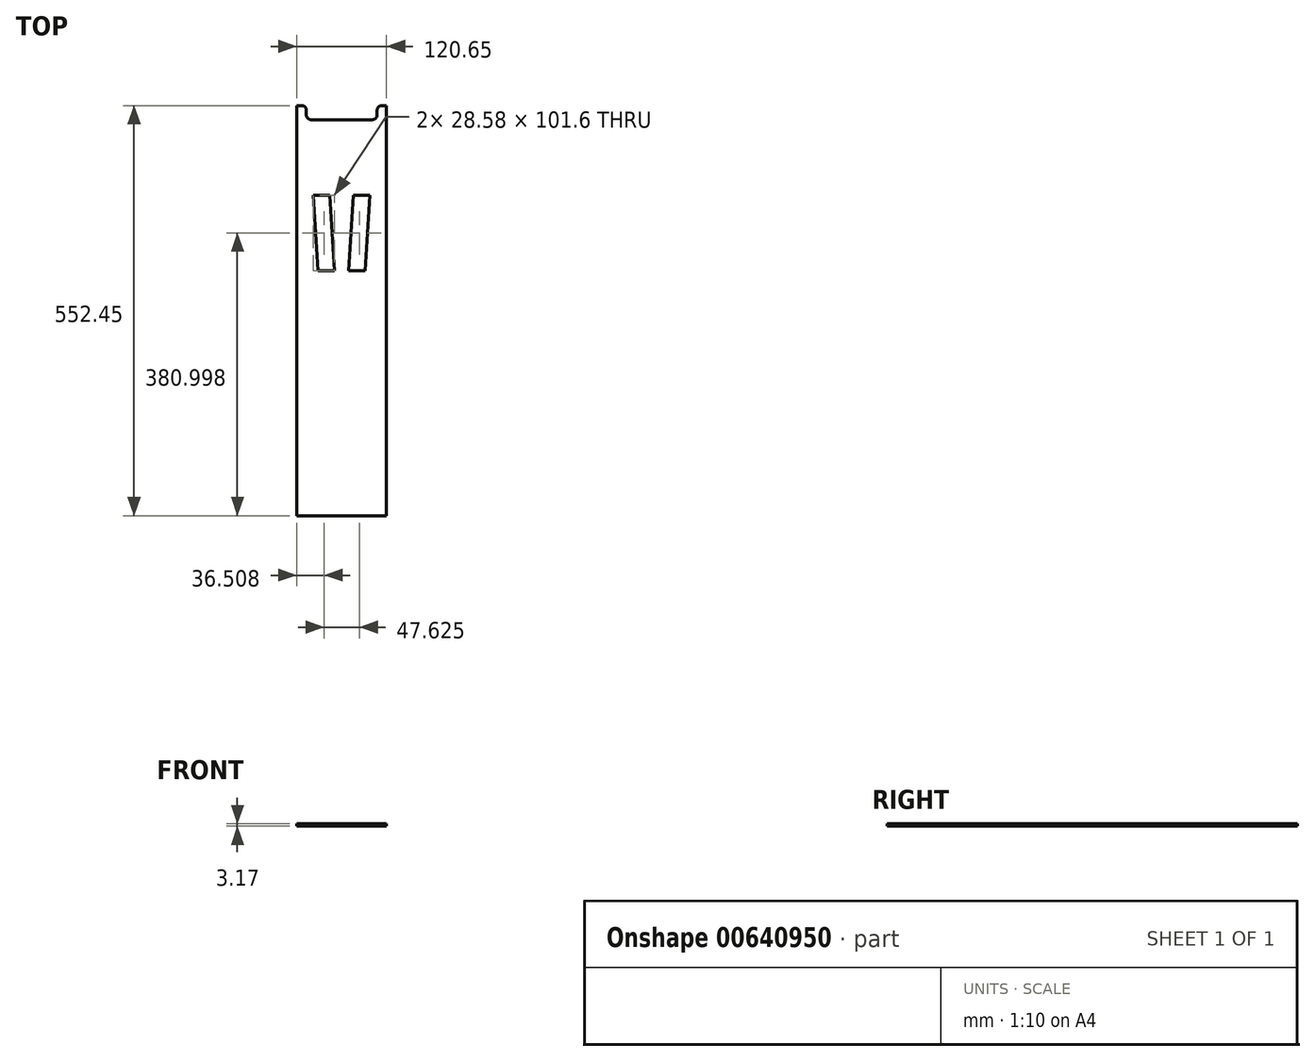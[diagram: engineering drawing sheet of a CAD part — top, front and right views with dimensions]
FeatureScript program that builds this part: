
annotation { "Feature Type Name" : "Feature", "Feature Type Description" : "" }
export const myFeature = defineFeature(function(context is Context, id is Id, definition is map)
    precondition{}
    {
        {
            var Q0;
            Q0=qCreatedBy(makeId("Top.planeOp"),FACE);
            var sketch = newSketch(context, id + "F0", { "sketchPlane" : qUnion([Q0])});
            skLineSegment(sketch, "E0", {"start": v(0, -170.62) * mm, "end": v(-60.33, -170.62) * mm});
            skLineSegment(sketch, "E1", {"start": v(-60.33, -170.62) * mm, "end": v(-60.33, 381.83) * mm});
            skLineSegment(sketch, "E2", {"start": v(-60.33, 381.83) * mm, "end": v(-53.98, 381.83) * mm});
            skLineSegment(sketch, "E3", {"start": v(-47.63, 375.48) * mm, "end": v(-47.63, 369.13) * mm});
            skLineSegment(sketch, "E4", {"start": v(-41.28, 362.78) * mm, "end": v(0, 362.78) * mm});
            skLineSegment(sketch, "E5", {"start": v(0, -249.15) * mm, "end": v(0, 463.94) * mm});
            skLineSegment(sketch, "E6", {"start": v(-9.53, 159.58) * mm, "end": v(-31.75, 159.58) * mm});
            skLineSegment(sketch, "E7", {"start": v(-31.75, 159.58) * mm, "end": v(-38.1, 261.18) * mm});
            skLineSegment(sketch, "E8", {"start": v(-38.1, 261.18) * mm, "end": v(-15.88, 261.18) * mm});
            skLineSegment(sketch, "E9", {"start": v(-15.88, 261.18) * mm, "end": v(-9.53, 159.58) * mm});
            skLineSegment(sketch, "E10.MirrorCS", {"start": v(47.62, 375.48) * mm, "end": v(47.62, 369.13) * mm});
            skLineSegment(sketch, "E11.MirrorCS", {"start": v(60.33, 381.83) * mm, "end": v(53.97, 381.83) * mm});
            skLineSegment(sketch, "E12.MirrorCS", {"start": v(9.53, 159.58) * mm, "end": v(31.75, 159.58) * mm});
            skLineSegment(sketch, "E13.MirrorCS", {"start": v(38.1, 261.18) * mm, "end": v(15.88, 261.18) * mm});
            skLineSegment(sketch, "E14.MirrorCS", {"start": v(41.27, 362.78) * mm, "end": v(0, 362.78) * mm});
            skLineSegment(sketch, "E15.MirrorCS", {"start": v(15.88, 261.18) * mm, "end": v(9.53, 159.58) * mm});
            skLineSegment(sketch, "E16.MirrorCS", {"start": v(31.75, 159.58) * mm, "end": v(38.1, 261.18) * mm});
            skLineSegment(sketch, "E17.MirrorCS", {"start": v(60.33, -170.62) * mm, "end": v(60.33, 381.83) * mm});
            skLineSegment(sketch, "E18.MirrorCS", {"start": v(0, -170.62) * mm, "end": v(60.33, -170.62) * mm});
            skPoint(sketch, "E19.visualSharp", {"position": v(-47.63, 381.83) * mm});
            skArc(sketch, "E19.filletArc", {"start": v(-47.63, 375.48) * mm, "mid": v(-49.48, 379.97) * mm, "end": v(-53.98, 381.83) * mm});
            skPoint(sketch, "E20.visualSharp", {"position": v(-47.63, 362.78) * mm});
            skArc(sketch, "E20.filletArc", {"start": v(-47.63, 369.13) * mm, "mid": v(-45.77, 364.64) * mm, "end": v(-41.28, 362.78) * mm});
            skPoint(sketch, "E21.visualSharp", {"position": v(47.63, 381.83) * mm});
            skArc(sketch, "E21.filletArc", {"start": v(53.97, 381.83) * mm, "mid": v(49.48, 379.97) * mm, "end": v(47.62, 375.48) * mm});
            skPoint(sketch, "E22.visualSharp", {"position": v(47.62, 362.78) * mm});
            skArc(sketch, "E22.filletArc", {"start": v(41.27, 362.78) * mm, "mid": v(45.77, 364.64) * mm, "end": v(47.62, 369.13) * mm});
            skSolve(sketch);
        }
        {
            var Q0;
            {var subQ0=sQuery(id+"F0.wireOp",EDGE,"E0");Q0=makeQuery(id+"F0.imprint","IMPRINT",FACE,{"disambiguationData":[TD([[makeQuery(id+"F0.imprint","IMPRINT",EDGE,{"derivedFrom":subQ0}),-1.0]])]});}
            var Q1;
            Q1=makeQuery(id+"F0.imprint","IMPRINT",FACE,{"disambiguationData":[TD([[makeQuery(id+"F0.imprint","IMPRINT",EDGE,{"derivedFrom":sQuery(id+"F0.wireOp",EDGE,"E10.MirrorCS")}),1.0]])]});
            extrude(context, id + "F1", {"entities" : qUnion([Q0, Q1]), "depth" : 3.17 * mm, "offsetDistance" : 25.4 * mm});
        }
    });
